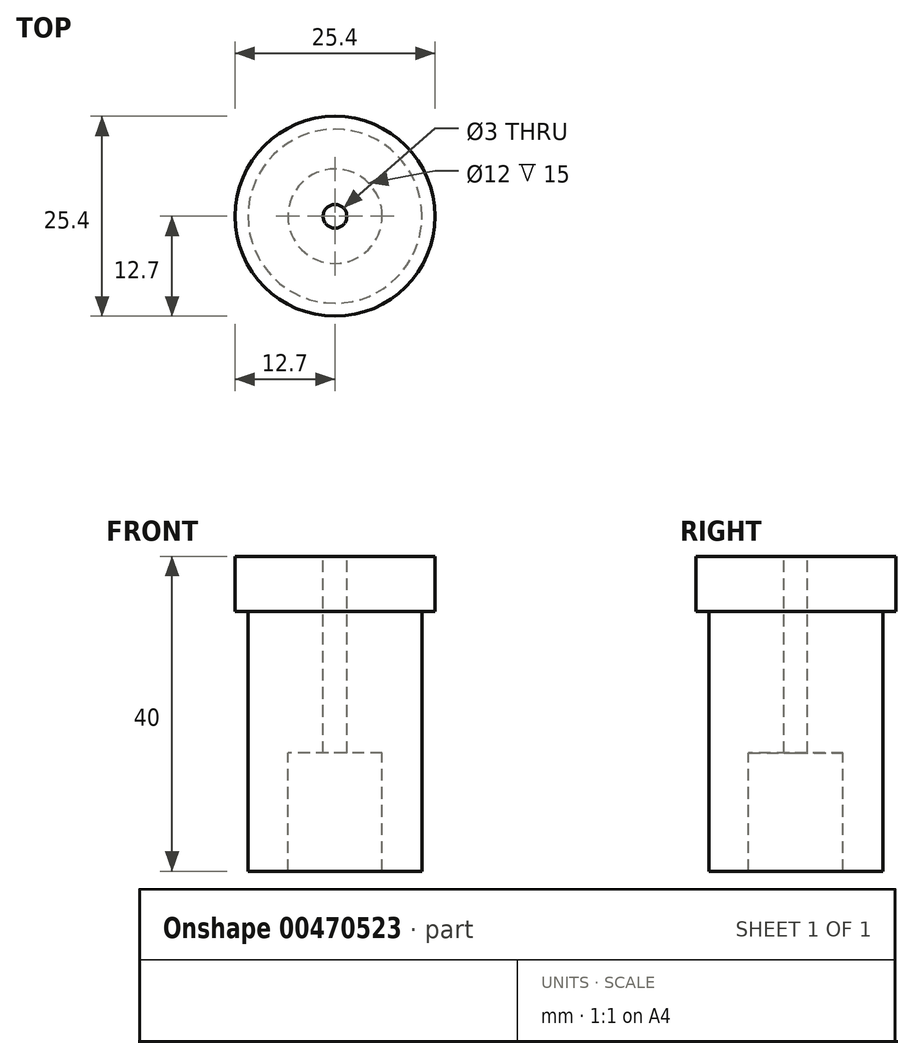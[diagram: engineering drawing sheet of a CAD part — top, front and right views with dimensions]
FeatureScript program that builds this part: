
annotation { "Feature Type Name" : "Feature", "Feature Type Description" : "" }
export const myFeature = defineFeature(function(context is Context, id is Id, definition is map)
    precondition{}
    {
        {
            var Q0;
            Q0=qCreatedBy(makeId("Front.planeOp"),FACE);
            var sketch = newSketch(context, id + "F0", { "sketchPlane" : qUnion([Q0])});
            skLineSegment(sketch, "E0", {"start": v(1.5, 38.98) * mm, "end": v(1.5, 13.98) * mm});
            skLineSegment(sketch, "E1", {"start": v(1.5, 13.98) * mm, "end": v(6, 13.98) * mm});
            skLineSegment(sketch, "E2", {"start": v(6, 13.98) * mm, "end": v(6, -1.02) * mm});
            skLineSegment(sketch, "E3", {"start": v(6, -1.02) * mm, "end": v(11.05, -1.02) * mm});
            skLineSegment(sketch, "E4", {"start": v(11.05, -1.02) * mm, "end": v(11.05, 31.98) * mm});
            skLineSegment(sketch, "E5", {"start": v(11.05, 31.98) * mm, "end": v(12.7, 31.98) * mm});
            skLineSegment(sketch, "E6", {"start": v(12.7, 31.98) * mm, "end": v(12.7, 38.98) * mm});
            skLineSegment(sketch, "E7", {"start": v(12.7, 38.98) * mm, "end": v(1.5, 38.98) * mm});
            skLineSegment(sketch, "E8", {"start": v(0, 63.82) * mm, "end": v(0, -29.04) * mm, "construction": true});
            skSolve(sketch);
        }
        {
            var Q0;
            Q0=makeQuery(id+"F0.imprint","IMPRINT",FACE,{"disambiguationData":[TD([[makeQuery(id+"F0.imprint","IMPRINT",EDGE,{"derivedFrom":sQuery(id+"F0.wireOp",EDGE,"E0")}),1.0]])]});
            var Q1;
            Q1=sQuery(id+"F0.wireOp",EDGE,"E8");
            revolve(context, id + "F1", {"entities" : qUnion([Q0]), "axis" : qUnion([Q1]), "revolveType" : RevolveType.FULL});
        }
    });
